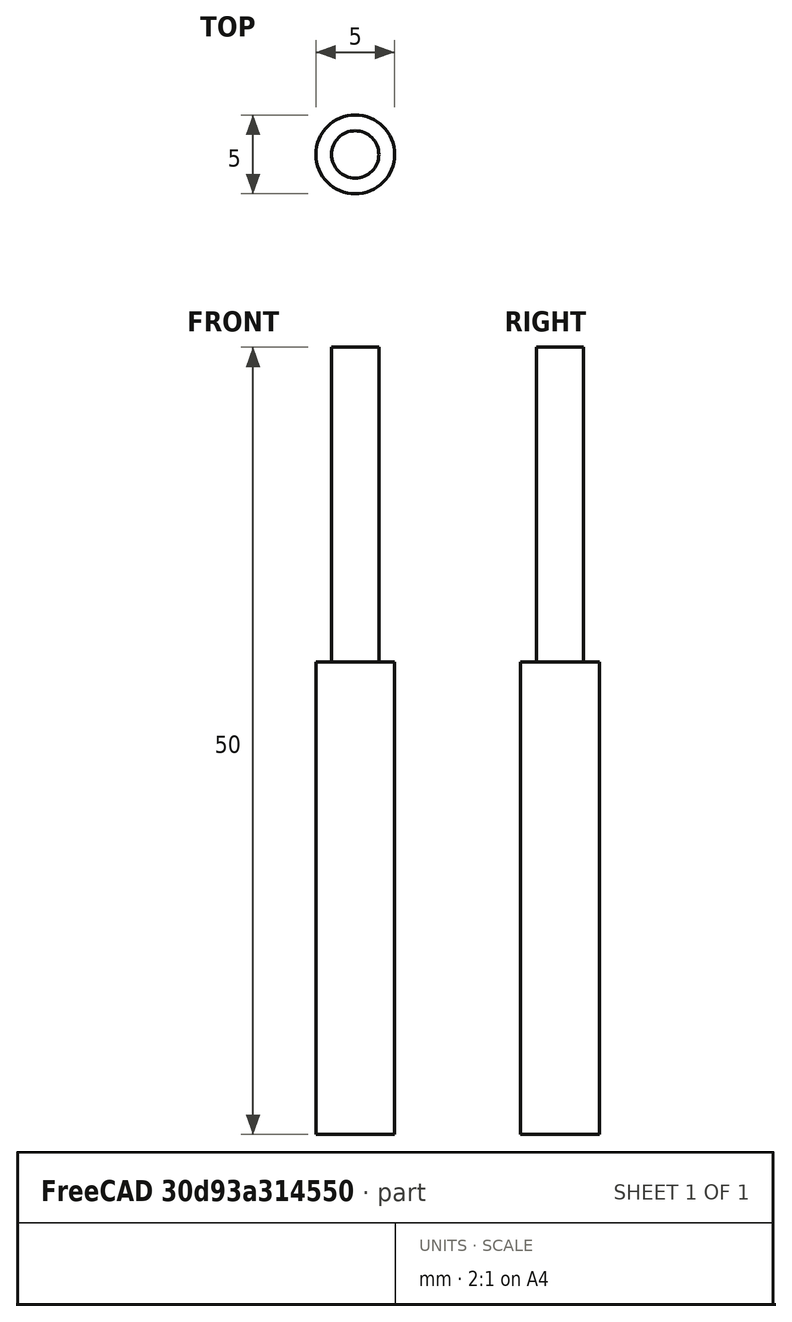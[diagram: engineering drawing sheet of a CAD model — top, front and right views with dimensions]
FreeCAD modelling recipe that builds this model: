
FCSTD DOCUMENT  (FreeCAD 0.21R32460 (Git))
Label: endmill
License: Creative Commons Attribution 4.0
LicenseURL: https://creativecommons.org/licenses/by/4.0/
objects: Sketcher::SketchObject×1, PartDesign::Revolution×1, App::FeaturePython×1, PartDesign::Body×1
note: 4 computed .brp shape members not serialized (recipe doc carries the construction recipe); baked Part::Feature solids carry a one-line shape summary decoded from their .brp

FEATURE [Sketcher::SketchObject] Sketch
  FullyConstrained = true
  MapMode = 5
  Placement = pos=(0,0,0) rot=(1,0,0;1.5708rad)
  Support = -> [XZ_Plane]
  expr: Constraints[10] = <<Attributes>>.Length
  expr: Constraints[16] = <<Attributes>>.ShankDiameter
  expr: Constraints[18] = <<Attributes>>.CuttingEdgeHeight
  expr: Constraints[9] = <<Attributes>>.Diameter
  sketch-geometry (8):
    g0: LineSegment StartX=0 StartY=50 StartZ=0 EndX=0 EndY=0 EndZ=0
    g1: LineSegment StartX=0 StartY=0 StartZ=0 EndX=2.5 EndY=0 EndZ=0
    g2: LineSegment StartX=2.5 StartY=0 StartZ=0 EndX=2.5 EndY=30 EndZ=0
    g3: LineSegment StartX=1.5 StartY=50 StartZ=0 EndX=0 EndY=50 EndZ=0
    g4: LineSegment StartX=2.5 StartY=0 StartZ=0 EndX=-2.5 EndY=0 EndZ=0
    g5: LineSegment StartX=1.5 StartY=29.99 StartZ=0 EndX=2.5 EndY=30 EndZ=0
    g6: LineSegment StartX=1.5 StartY=50 StartZ=0 EndX=1.5 EndY=29.99 EndZ=0
    g7: LineSegment StartX=-1.5 StartY=50 StartZ=0 EndX=1.5 EndY=50 EndZ=0
  constraints (21):
    c: Vertical(g0)
    c: Coincident(g0,g1)
    c: Horizontal(g1)
    c: Coincident(g1,g2)
    c: Vertical(g2)
    c: Horizontal(g3)
    c: Coincident(g0,g3)
    c: Coincident(g4,g1)
    c: Symmetric(g1,g4,g0)
    c: DistanceX(g4,g4) = 5
    c: DistanceY(g2,g3) = 50
    c: Coincident(g2,g5)
    c: Vertical(g6)
    c: Coincident(g3,g6)
    c: Symmetric(g7,g7,g0)
    c: Coincident(g7,g3)
    c: DistanceX(g7,g7) = 3
    c: Coincident(g5,g6)
    c: DistanceY(g2) = 30
    c: Coincident(g0,g-1)
    c: DistanceY(g5,g2) = 0.01
FEATURE [PartDesign::Revolution] Revolution
  AllowMultiFace = false
  Angle = 360
  Axis = (0,-2e-16,1)
  Base = (0,0,0)
  Placement = pos=(0,0,0) rot=(1,0,0;1.5708rad)
  Profile = -> Sketch
  ReferenceAxis = -> Sketch [V_Axis]
  Reversed = true
FEATURE [App::FeaturePython] PropertyBag  label="Attributes"  # WARN: FeaturePython — macro-defined, semantics opaque (R4)
  Chipload = 0
  CustomPropertyGroups = Attributes | Shape
  CuttingEdgeHeight = 30
  Diameter = 5
  Flutes = 0
  Length = 50
  Material = 0
  ShankDiameter = 3
  SpindleDirection = 0
FEATURE [PartDesign::Body] Body  label="Endmill"
  Group = -> [Sketch,Revolution,PropertyBag]
  Origin = -> Origin
  Tip = -> Revolution
